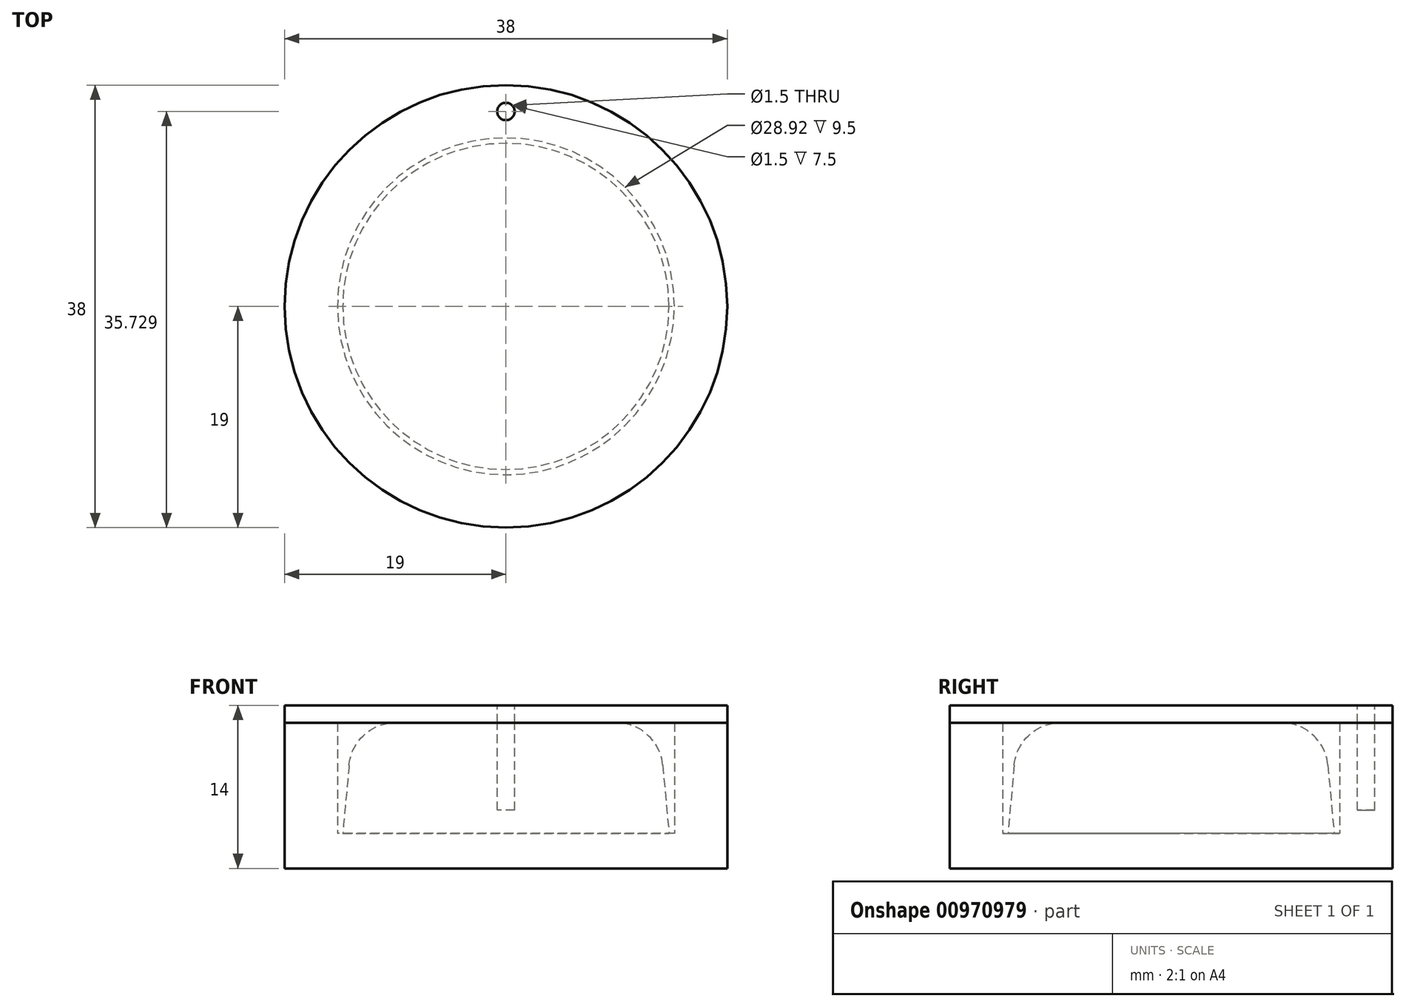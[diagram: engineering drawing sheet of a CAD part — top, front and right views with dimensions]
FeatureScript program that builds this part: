
annotation { "Feature Type Name" : "Feature", "Feature Type Description" : "" }
export const myFeature = defineFeature(function(context is Context, id is Id, definition is map)
    precondition{}
    {
        {
            var Q0;
            Q0=qCreatedBy(makeId("Front.planeOp"),FACE);
            var sketch = newSketch(context, id + "F0", { "sketchPlane" : qUnion([Q0])});
            skLineSegment(sketch, "E0", {"start": v(0, 0) * mm, "end": v(0, 14.6) * mm, "construction": true});
            skLineSegment(sketch, "E1", {"start": v(0, 0) * mm, "end": v(14, 0) * mm});
            skLineSegment(sketch, "E2", {"start": v(14, 0) * mm, "end": v(13.12, 9.5) * mm});
            skLineSegment(sketch, "E3", {"start": v(13.12, 9.5) * mm, "end": v(0, 9.5) * mm});
            skLineSegment(sketch, "E4", {"start": v(0, 9.5) * mm, "end": v(0, 0) * mm, "construction": true});
            skLineSegment(sketch, "E5", {"start": v(0, 0) * mm, "end": v(0, 9.5) * mm});
            skSolve(sketch);
        }
        {
            var Q0;
            Q0 = qSketchRegion(id + "F0", true);
            var Q1;
            Q1=sQuery(id+"F0.wireOp",EDGE,"E0");
            revolve(context, id + "F1", {"surfaceOperationType" : NewSurfaceOperationType.NEW, "entities" : qUnion([Q0]), "axis" : qUnion([Q1]), "revolveType" : RevolveType.FULL});
        }
        {
            var Q0;
            Q0=makeQuery(id+"F1.opRevolve","SWEPT_EDGE",EDGE,{"disambiguationData":[OSD([sQuery(id+"F0.wireOp",EDGE,"E2"),sQuery(id+"F0.wireOp",EDGE,"E3")])]});
            fillet(context, id + "F2", {"entities" : qUnion([Q0]), "radius" : 4 * mm, "tangentPropagation" : true, "allowEdgeOverflow" : false});
        }
        {
            var Q0;
            Q0=qCreatedBy(makeId("Top.planeOp"),FACE);
            var sketch = newSketch(context, id + "F3", { "sketchPlane" : qUnion([Q0])});
            skCircle(sketch, "E6", {"center": v(0, 0) * mm, "radius": 19 * mm});
            skSolve(sketch);
        }
        {
            var Q0;
            Q0 = qSketchRegion(id + "F3", true);
            extrude(context, id + "F4", {"entities" : qUnion([Q0]), "oppositeDirection" : true, "depth" : 3 * mm, "offsetDistance" : 25 * mm});
        }
        {
            var Q0;
            Q0=makeQuery(id+"F4.opExtrude","CAP_FACE",FACE,{"disambiguationData":[OSD([sQuery(id+"F3.wireOp",EDGE,"E6")])],"isStart":true});
            var sketch = newSketch(context, id + "F5", { "sketchPlane" : qUnion([Q0])});
            skCircle(sketch, "E7", {"center": v(0, 0) * mm, "radius": 14.46 * mm});
            skCircle(sketch, "E8.0", {"center": v(0, 0) * mm, "radius": 19 * mm});
            skSolve(sketch);
        }
        {
            var Q0;
            Q0 = qSketchRegion(id + "F5", true);
            var Q1;
            Q1=makeQuery(id+"F1.opRevolve","SWEPT_FACE",FACE,{"disambiguationData":[OSD([sQuery(id+"F0.wireOp",EDGE,"E3")])]});
            extrude(context, id + "F6", {"entities" : qUnion([Q0]), "operationType" : NewBodyOperationType.ADD, "endBound" : BoundingType.UP_TO_SURFACE, "depth" : 10 * mm, "endBoundEntityFace" : qUnion([Q1]), "offsetDistance" : 25 * mm});
        }
        {
            var Q0;
            Q0=makeQuery(id+"F6.opExtrude","CAP_FACE",FACE,{"disambiguationData":[OSD([sQuery(id+"F5.wireOp",EDGE,"E7"),sQuery(id+"F5.wireOp",EDGE,"E8.0")])],"isStart":false});
            var sketch = newSketch(context, id + "F7", { "sketchPlane" : qUnion([Q0])});
            skCircle(sketch, "E9.0", {"center": v(0, 0) * mm, "radius": 19 * mm});
            skSolve(sketch);
        }
        {
            var Q0;
            Q0 = qSketchRegion(id + "F7", true);
            extrude(context, id + "F8", {"entities" : qUnion([Q0]), "depth" : 1.5 * mm, "offsetDistance" : 25 * mm});
        }
        {
            var Q0;
            Q0=makeQuery(id+"F8.opExtrude","CAP_FACE",FACE,{"disambiguationData":[OSD([sQuery(id+"F7.wireOp",EDGE,"E9.0")])],"isStart":false});
            var sketch = newSketch(context, id + "F9", { "sketchPlane" : qUnion([Q0])});
            skCircle(sketch, "E10", {"center": v(0, 16.73) * mm, "radius": 0.75 * mm});
            skCircle(sketch, "E11", {"center": v(0, 0) * mm, "radius": 16.73 * mm, "construction": true});
            skLineSegment(sketch, "E12", {"start": v(0, 14.46) * mm, "end": v(0, 19) * mm, "construction": true});
            skSolve(sketch);
        }
        {
            var Q0;
            Q0 = qSketchRegion(id + "F9", true);
            extrude(context, id + "F10", {"entities" : qUnion([Q0]), "operationType" : NewBodyOperationType.REMOVE, "oppositeDirection" : true, "depth" : 9 * mm, "offsetDistance" : 25 * mm});
        }
    });
